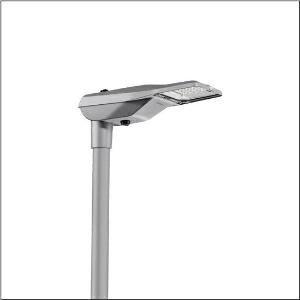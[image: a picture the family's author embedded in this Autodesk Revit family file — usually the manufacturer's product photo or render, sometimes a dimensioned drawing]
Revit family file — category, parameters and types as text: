
# Revit family: streetlight_sl_21_iq_micro___st1_0ab_5xe1m31y08db_79d8
name_source: partatom
category: Lighting Fixtures
units: mm (PartAtom-declared; Revit-internal decimal feet)

## family parameters
Cut with Voids When Loaded = No
Host = Face
Light Source = No
Part Type = Normal
Room Calculation Point = No
Round Connector Dimension = Use Diameter
Shared = No

## types (1)
- --- (1 x LED, 4490 lm, 39.1 W, 3000K)
    Apparent Load = 39 VA
    CIE Flux Codes = 38 73 97 100 100
    Color Rendering = 70
    Color Temperature = 3000K
    Default Elevation = 1800 mm
    Description = Streetlight SL 21 iQ micro, mast luminaire, primary light control with lens, of PMMA, primary optical cover: cover, of toughened safety glass, transparent, light distribution: ST1.0aB, light emission: direct distribution, primary light characteristic: asymmetric, installation type: post-top, side-entry, LED, High Power LED, rated luminous flux: 4.490lm, luminous efficacy: 115lm/W, light colour: 730, colour temperature: 3000K, control: presetting dimming logarithmic, Street-Remote, Auto-Match, Temp-Guard, Lumen-Switch, Night-Set, Smart-Wire, Light-Fading, Desk-Remote (wireless, voltage-free reading and setting of iQ features in the workshop via application-optimized NFC function/RFID function), optimised constant luminous flux control (CLO 2.0), mains connection: 220..240V, AC, 50/60Hz, start of lifetime: 39W, end of service life: 41W, reduction: 17W, luminaire housing, of diecast aluminium, powder-coated, Siteco® metallic grey (DB 702S), corrosivity category C5 mid according to DIN EN ISO 12944, please order mast flange separately, inclination adjustable: 0°, 5°, 10°, 15°, sealing non-destructively replaceable, multi-level sealing system, length: 528mm, width: 235mm, height: 110mm, mast flange for spigot size: 42mm (side-entry): 5XC10008XM4, 60/48mm (side-entry/post-top): 5XC10108XM2, 76/60mm (side-entry/post-top): 5XC10108XM1, Smart Interface below and above, protection rating (complete): IP66, insulation class (complete): insulation class II (safety insulation), certification: CE, ENEC, ENEC+, VDE, impact resistance: IK09, permissible operating ambient temperature for outdoor applications: -40..+50°C, standard-compliant lighting for roads and squares, packaging unit: 1 piece

Light Distribution: ST1.0aB
    Height = 110 mm
    Lamp = 1 x LED
    Lamp Light Flux = 4490 lm
    Lamp Power = 39.1 W
    Lamp count = 1
    Length = 528 mm
    Luminous efficacy = 115 lm/W
    Manufacturer = Siteco
    ModVariant = No
    Model = 5XE1M31Y08DB
    Number of Poles = 1
    OnlyDefault = Yes
    Power Factor = 1
    Product Name = Streetlight SL 21 iQ micro | ST1.0aB
    Product group = mast luminaire | pylon top
    ProductGroupID = 6100
    Protection Class = Protection class II
    Protection Degree = IP 66
    RLX_Detail_Level = 1
    RLX_Emergency_Light_Flux = 0 lm
    RLX_Emergency_Type = 0
    RLX_Emergency_Type_DB = No
    RlxData = <blob elided: 98293 chars, md5=91190cbb>
    Socket = socket
    Standby Power = 0 W
    System Light Flux = 4490 lm
    System Power = 39 W
    Type Comments = factory setting: luminous flux: 100 % | dim-lin: 254 | 765 mA
    Type Image = l_1007239.jpg
    URL = http://relux.com
    VarID = @adj_060875
    Voltage = 0 V
    Weight = 0.00 kg
    Width = 235 mm

## geometry (parser evidence)
native form markers: Blend x4, Sweep x11
no freeform markers — native parametric forms only
